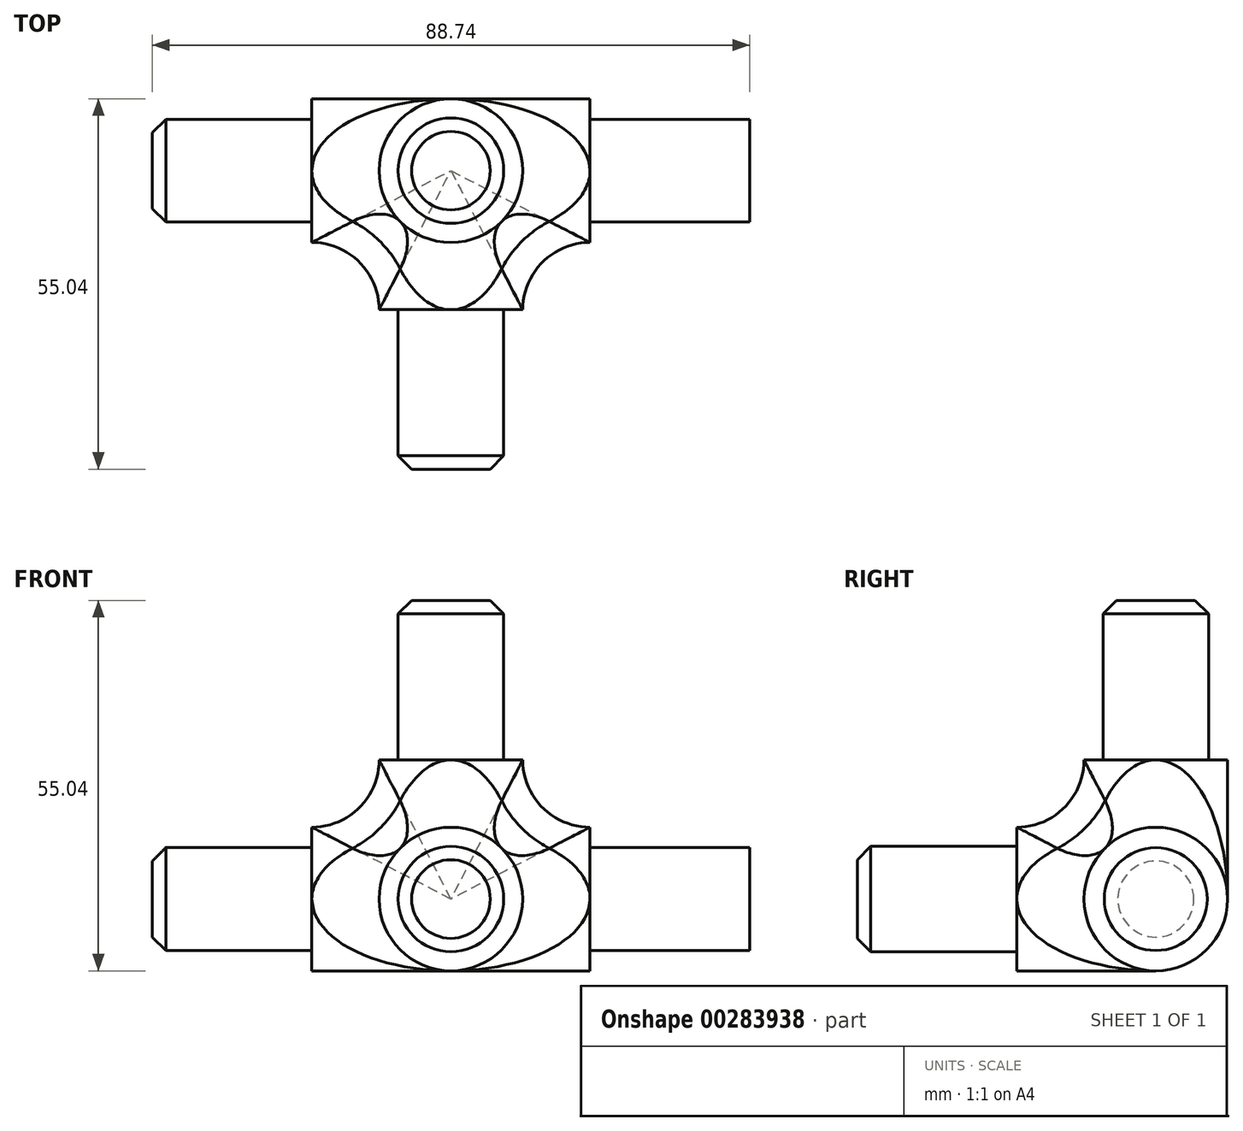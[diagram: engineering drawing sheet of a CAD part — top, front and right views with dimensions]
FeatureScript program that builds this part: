
annotation { "Feature Type Name" : "Feature", "Feature Type Description" : "" }
export const myFeature = defineFeature(function(context is Context, id is Id, definition is map)
    precondition{}
    {
        {
            var Q0;
            Q0=qCreatedBy(makeId("Right.planeOp"),FACE);
            var sketch = newSketch(context, id + "F0", { "sketchPlane" : qUnion([Q0])});
            skCircle(sketch, "E0", {"center": v(0, 0) * mm, "radius": 10.67 * mm});
            skSolve(sketch);
        }
        {
            var Q0;
            Q0=qSketchRegion(id+"F0",true);
            extrude(context, id + "F1", {"entities" : qUnion([Q0]), "endBound" : BoundingType.SYMMETRIC, "depth" : 21.34 * mm + 20 * mm});
        }
        {
            var Q0;
            Q0=makeQuery(id+"F1.opExtrude","CAP_FACE",FACE,{"disambiguationData":[OSD([sQuery(id+"F0.wireOp",EDGE,"E0")])],"isStart":false});
            var sketch = newSketch(context, id + "F2", { "sketchPlane" : qUnion([Q0])});
            skCircle(sketch, "E1", {"center": v(0, 0) * mm, "radius": 7.9 * mm});
            skSolve(sketch);
        }
        {
            var Q0;
            Q0=qSketchRegion(id+"F2",true);
            extrude(context, id + "F3", {"entities" : qUnion([Q0]), "operationType" : NewBodyOperationType.ADD, "depth" : 15.8 * mm * 1.5});
        }
        {
            var Q0;
            Q0=makeQuery(id+"F3.opExtrude","CAP_FACE",FACE,{"disambiguationData":[OSD([sQuery(id+"F2.wireOp",EDGE,"E1")])],"isStart":false});
            var sketch = newSketch(context, id + "F4", { "sketchPlane" : qUnion([Q0])});
            skCircle(sketch, "E2.0", {"center": v(0, 0) * mm, "radius": 7.9 * mm});
            skCircle(sketch, "E3", {"center": v(0, 0) * mm, "radius": 7.65 * mm});
            skSolve(sketch);
        }
        {
            var Q0;
            Q0=qSketchRegion(id+"F4",true);
            var Q1;
            Q1=makeQuery(id+"F1.opExtrude","CAP_FACE",FACE,{"disambiguationData":[OSD([sQuery(id+"F0.wireOp",EDGE,"E0")])],"isStart":false});
            extrude(context, id + "F5", {"entities" : qUnion([Q0]), "operationType" : NewBodyOperationType.REMOVE, "endBound" : BoundingType.UP_TO_SURFACE, "oppositeDirection" : true, "endBoundEntityFace" : qUnion([Q1]), "depth" : 25 * mm});
        }
        {
            var Q0;
            Q0=makeQuery(id+"F1.opExtrude","CAP_FACE",FACE,{"disambiguationData":[OSD([sQuery(id+"F0.wireOp",EDGE,"E0")])],"isStart":true});
            var sketch = newSketch(context, id + "F6", { "sketchPlane" : qUnion([Q0])});
            skCircle(sketch, "E4", {"center": v(0, 0) * mm, "radius": 7.65 * mm});
            skSolve(sketch);
        }
        {
            var Q0;
            Q0=qSketchRegion(id+"F6",true);
            extrude(context, id + "F7", {"entities" : qUnion([Q0]), "operationType" : NewBodyOperationType.ADD, "depth" : 15.8 * mm * 1.5});
        }
        {
            var Q0;
            Q0=qCreatedBy(makeId("Top.planeOp"),FACE);
            var sketch = newSketch(context, id + "F8", { "sketchPlane" : qUnion([Q0])});
            skCircle(sketch, "E5", {"center": v(0, 0) * mm, "radius": 10.67 * mm});
            skSolve(sketch);
        }
        {
            var Q0;
            Q0=qSketchRegion(id+"F8",true);
            extrude(context, id + "F9", {"entities" : qUnion([Q0]), "operationType" : NewBodyOperationType.ADD, "depth" : 21.34 * mm / 2 + 10 * mm});
        }
        {
            var Q0;
            Q0=makeQuery(id+"F9.opExtrude","CAP_FACE",FACE,{"disambiguationData":[OSD([sQuery(id+"F8.wireOp",EDGE,"E5")])],"isStart":false});
            var sketch = newSketch(context, id + "F10", { "sketchPlane" : qUnion([Q0])});
            skCircle(sketch, "E6", {"center": v(0, 0) * mm, "radius": 7.84 * mm});
            skSolve(sketch);
        }
        {
            var Q0;
            Q0=qSketchRegion(id+"F10",true);
            extrude(context, id + "F11", {"entities" : qUnion([Q0]), "operationType" : NewBodyOperationType.ADD, "depth" : 15.8 * mm * 1.5});
        }
        {
            var Q0;
            Q0=qCreatedBy(makeId("Front.planeOp"),FACE);
            var sketch = newSketch(context, id + "F12", { "sketchPlane" : qUnion([Q0])});
            skCircle(sketch, "E7", {"center": v(0, 0) * mm, "radius": 10.67 * mm});
            skSolve(sketch);
        }
        {
            var Q0;
            Q0 = qSketchRegion(id + "F12", true);
            extrude(context, id + "F13", {"entities" : qUnion([Q0]), "operationType" : NewBodyOperationType.ADD, "depth" : 21.34 * mm / 2 + 10 * mm});
        }
        {
            var Q0;
            Q0=makeQuery(id+"F13.opExtrude","CAP_FACE",FACE,{"disambiguationData":[OSD([sQuery(id+"F12.wireOp",EDGE,"E7")])],"isStart":false});
            var sketch = newSketch(context, id + "F14", { "sketchPlane" : qUnion([Q0])});
            skCircle(sketch, "E8", {"center": v(0, 0) * mm, "radius": 7.84 * mm});
            skSolve(sketch);
        }
        {
            var Q0;
            Q0 = qSketchRegion(id + "F14", true);
            extrude(context, id + "F15", {"entities" : qUnion([Q0]), "operationType" : NewBodyOperationType.ADD, "depth" : 15.8 * mm * 1.5});
        }
        {
            var Q0;
            Q0=makeQuery(id+"F11.opExtrude","CAP_EDGE",EDGE,{"disambiguationData":[OSD([sQuery(id+"F10.wireOp",EDGE,"E6")])],"isStart":false});
            var Q1;
            Q1=makeQuery(id+"F5.boolean.opBoolean","COPY",EDGE,{"derivedFrom":makeQuery(id+"F5.opExtrude","CAP_EDGE",EDGE,{"disambiguationData":[OSD([sQuery(id+"F4.wireOp",EDGE,"E3")])],"isStart":true})});
            var Q2;
            Q2=makeQuery(id+"F7.opExtrude","CAP_EDGE",EDGE,{"disambiguationData":[OSD([sQuery(id+"F6.wireOp",EDGE,"E4")])],"isStart":false});
            var Q3;
            Q3=makeQuery(id+"F15.opExtrude","CAP_EDGE",EDGE,{"disambiguationData":[OSD([sQuery(id+"F14.wireOp",EDGE,"E8")])],"isStart":false});
            chamfer(context, id + "F16", {"entities" : qUnion([Q0, Q1, Q2, Q3]), "width" : 2 * mm, "tangentPropagation" : true});
        }
        {
            var Q0;
            Q0=makeQuery(id+"F9.boolean.opBoolean","INTERSECT",EDGE,{"disambiguationData":[OD(0.0)],"derivedFrom":[makeQuery(id+"F1.opExtrude","SWEPT_FACE",FACE,{"disambiguationData":[OSD([sQuery(id+"F0.wireOp",EDGE,"E0")])]}),makeQuery(id+"F9.opExtrude","SWEPT_FACE",FACE,{"disambiguationData":[OSD([sQuery(id+"F8.wireOp",EDGE,"E5")])]})]});
            var Q1;
            Q1=makeQuery(id+"F13.boolean.opBoolean","INTERSECT",EDGE,{"disambiguationData":[OD(0.0)],"derivedFrom":[makeQuery(id+"F1.opExtrude","SWEPT_FACE",FACE,{"disambiguationData":[OSD([sQuery(id+"F0.wireOp",EDGE,"E0")])]}),makeQuery(id+"F13.opExtrude","SWEPT_FACE",FACE,{"disambiguationData":[OSD([sQuery(id+"F12.wireOp",EDGE,"E7")])]})]});
            var Q2;
            Q2=makeQuery(id+"F13.boolean.opBoolean","INTERSECT",EDGE,{"disambiguationData":[OD(1.0)],"derivedFrom":[makeQuery(id+"F1.opExtrude","SWEPT_FACE",FACE,{"disambiguationData":[OSD([sQuery(id+"F0.wireOp",EDGE,"E0")])]}),makeQuery(id+"F13.opExtrude","SWEPT_FACE",FACE,{"disambiguationData":[OSD([sQuery(id+"F12.wireOp",EDGE,"E7")])]})]});
            var Q3;
            Q3=makeQuery(id+"F9.boolean.opBoolean","INTERSECT",EDGE,{"disambiguationData":[OD(1.0)],"derivedFrom":[makeQuery(id+"F1.opExtrude","SWEPT_FACE",FACE,{"disambiguationData":[OSD([sQuery(id+"F0.wireOp",EDGE,"E0")])]}),makeQuery(id+"F9.opExtrude","SWEPT_FACE",FACE,{"disambiguationData":[OSD([sQuery(id+"F8.wireOp",EDGE,"E5")])]})]});
            var Q4;
            Q4=makeQuery(id+"F13.boolean.opBoolean","INTERSECT",EDGE,{"derivedFrom":[makeQuery(id+"F9.opExtrude","SWEPT_FACE",FACE,{"disambiguationData":[OSD([sQuery(id+"F8.wireOp",EDGE,"E5")])]}),makeQuery(id+"F13.opExtrude","SWEPT_FACE",FACE,{"disambiguationData":[OSD([sQuery(id+"F12.wireOp",EDGE,"E7")])]})]});
            fillet(context, id + "F17", {"entities" : qUnion([Q0, Q1, Q2, Q3, Q4]), "radius" : 10 * mm, "tangentPropagation" : true, "allowEdgeOverflow" : false});
        }
    });
